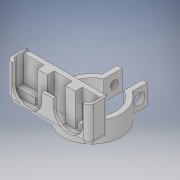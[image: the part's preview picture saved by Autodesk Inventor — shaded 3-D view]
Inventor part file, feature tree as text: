
AUTODESK INVENTOR PART (.ipt)
format: ipt  version: 2018 (Build 220112000, 112)  size: 330,240 bytes
history: native  units: in
note: dims shown in document units (in); Inventor stores cm internally (conversion verified against a paired STEP export)
features: extrude x8, sketch x8, fillet x3, reference x3, other x2, projected_geometry x1
ambient origin geometry x8: Origin, YZ Plane, XZ Plane, XY Plane, X Axis, Y Axis, Z Axis, Center Point
bodies: Solid1 (feature_tree)
feature tree (25):
  extrude  "Extrusion1"  Depth=0.125in
  extrude  "Extrusion2"  Depth=0.125in
  extrude  "Extrusion3"  Depth=0.125in
  extrude  "Extrusion4"  Depth=0.25in
  extrude  "Extrusion5"  Depth=0.194in
  extrude  "Extrusion7"  Depth=0.04in
  extrude  "Extrusion8"  Depth=0.8125in TaperAngle=0.0deg
  extrude  "Extrusion9"  Depth=0.125in
  fillet  "Fillet1"  Radius=0.05in
  fillet  "Fillet2"  Radius=0.05in
  fillet  "Fillet3"  Radius=0.05in
  sketch  "Sketch1"  dims[d0=1.19in d1=0.125in]
  sketch  "Sketch2"  dims[d2=0.125in d3=0.375in]
  sketch  "Sketch3"  dims[d4=1.0in d5=0.125in]
  sketch  "Sketch4"  dims[d6=0.5in d7=0.0in d8=0.25in]
  sketch  "Sketch5"  dims[d9=0.2in d10=0.194in]
  sketch  "Sketch7"  dims[d11=1.0in d12=0.0in d13=0.04in]
  projected_geometry  "Projected Loop3"
  sketch  "Sketch8"  dims[d14=1.0in d15=0.0in d18=0.8125in d19=0.0in]
  sketch  "Sketch9"  dims[d20=1.95in d21=0.975in d22=0.05in d23=0.05in d24=0.05in d25=0.05in d26=0.445in d27=0.0in d28=0.9125in d29=0.8in d30=0.05in d31=0.05in d35=0.17in d36=0.0in d37=0.25in d38=0.25in d39=0.5in d40=0.5in d41=0.17in d42=0.0in d43=0.05in d44=0.05in d45=0.0625in d46=0.0in d47=0.05in d48=0.125in d49=0.25in d50=0.125in]
  reference  "Reference1"
  reference  "Reference2"
  reference  "Reference3"
  other  "Assembly1"
  other  "Ultrasonic_sensor:1"
